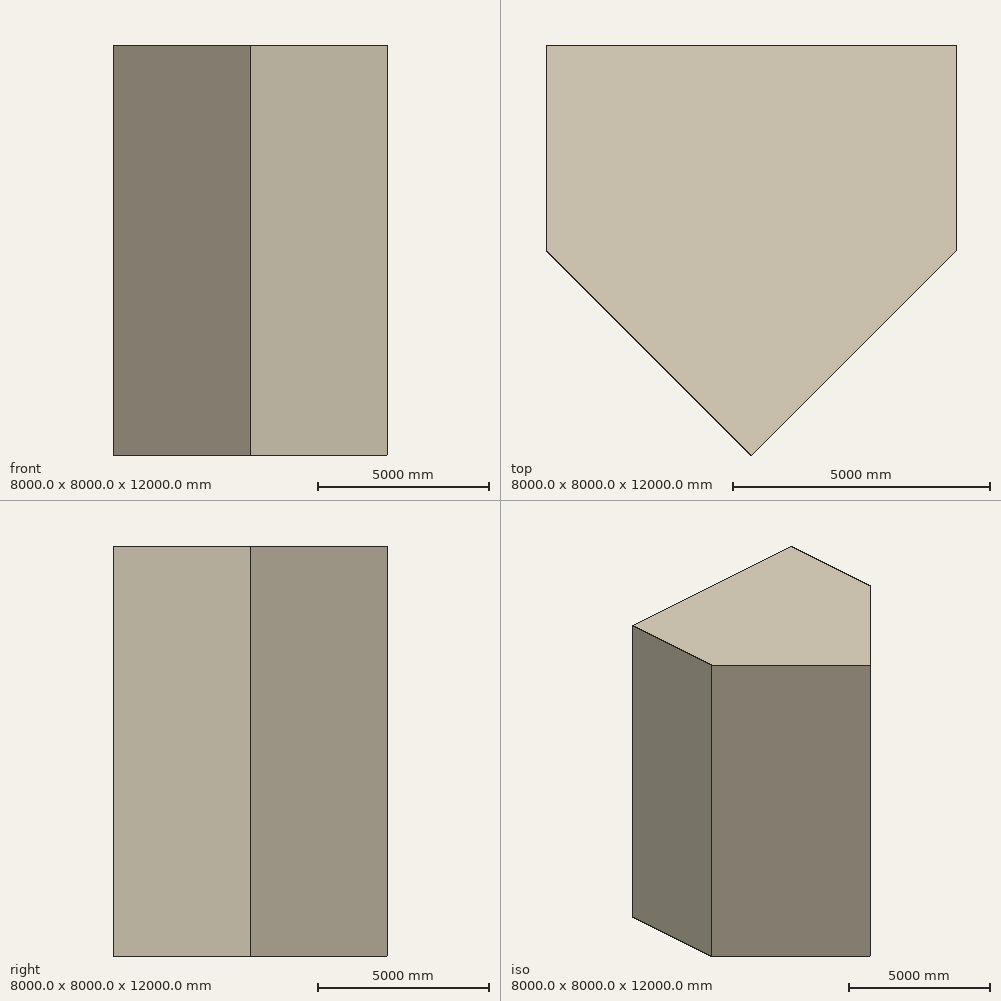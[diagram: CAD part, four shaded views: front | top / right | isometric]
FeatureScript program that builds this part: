
annotation { "Feature Type Name" : "Feature", "Feature Type Description" : "" }
export const myFeature = defineFeature(function(context is Context, id is Id, definition is map)
    precondition{}
    {
        {
            var Q0;
            Q0=qCreatedBy(makeId("Front.planeOp"),FACE);
            var sketch = newSketch(context, id + "F0", { "sketchPlane" : qUnion([Q0])});
            skLineSegment(sketch, "E0.bottom", {"start": v(-3999, 8376.4) * mm, "end": v(4001, 8376.4) * mm});
            skLineSegment(sketch, "E0.top", {"start": v(-3999, -3623.6) * mm, "end": v(4001, -3623.6) * mm});
            skLineSegment(sketch, "E0.left", {"start": v(-3999, 8376.4) * mm, "end": v(-3999, -3623.6) * mm});
            skLineSegment(sketch, "E0.right", {"start": v(4001, 8376.4) * mm, "end": v(4001, -3623.6) * mm});
            skSolve(sketch);
        }
        {
            var Q0;
            Q0 = qSketchRegion(id + "F0", true);
            extrude(context, id + "F1", {"entities" : qUnion([Q0]), "depth" : 8000 * mm});
        }
        {
            var Q0;
            Q0=makeQuery(id+"F1.opExtrude","SWEPT_FACE",FACE,{"disambiguationData":[OSD([sQuery(id+"F0.wireOp",EDGE,"E0.bottom")])]});
            var sketch = newSketch(context, id + "F2", { "sketchPlane" : qUnion([Q0])});
            skLineSegment(sketch, "E1", {"start": v(4001, -4000) * mm, "end": v(1, -8000) * mm});
            skLineSegment(sketch, "E2", {"start": v(4001, -8000) * mm, "end": v(4001, -4000) * mm});
            skLineSegment(sketch, "E3", {"start": v(4001, -8000) * mm, "end": v(1, -8000) * mm});
            skSolve(sketch);
        }
        {
            var Q0;
            Q0 = qSketchRegion(id + "F2", true);
            extrude(context, id + "F3", {"entities" : qUnion([Q0]), "operationType" : NewBodyOperationType.REMOVE, "endBound" : BoundingType.THROUGH_ALL, "oppositeDirection" : true, "depth" : 25 * mm});
        }
        {
            var Q0;
            Q0=makeQuery(id+"F1.opExtrude","SWEPT_FACE",FACE,{"disambiguationData":[OSD([sQuery(id+"F0.wireOp",EDGE,"E0.bottom")])]});
            var sketch = newSketch(context, id + "F4", { "sketchPlane" : qUnion([Q0])});
            skLineSegment(sketch, "E4", {"start": v(1, -8000) * mm, "end": v(-3999, -4000) * mm});
            skSolve(sketch);
        }
        {
            var Q0;
            {var subQ0=sQuery(id+"F4.wireOp",EDGE,"E4");Q0=makeQuery(id+"F4.imprint","IMPRINT",FACE,{"disambiguationData":[TD([[makeQuery(id+"F4.imprint","IMPRINT",EDGE,{"derivedFrom":subQ0}),1.0]])]});}
            extrude(context, id + "F5", {"entities" : qUnion([Q0]), "operationType" : NewBodyOperationType.REMOVE, "endBound" : BoundingType.THROUGH_ALL, "oppositeDirection" : true, "depth" : 25 * mm});
        }
    });
